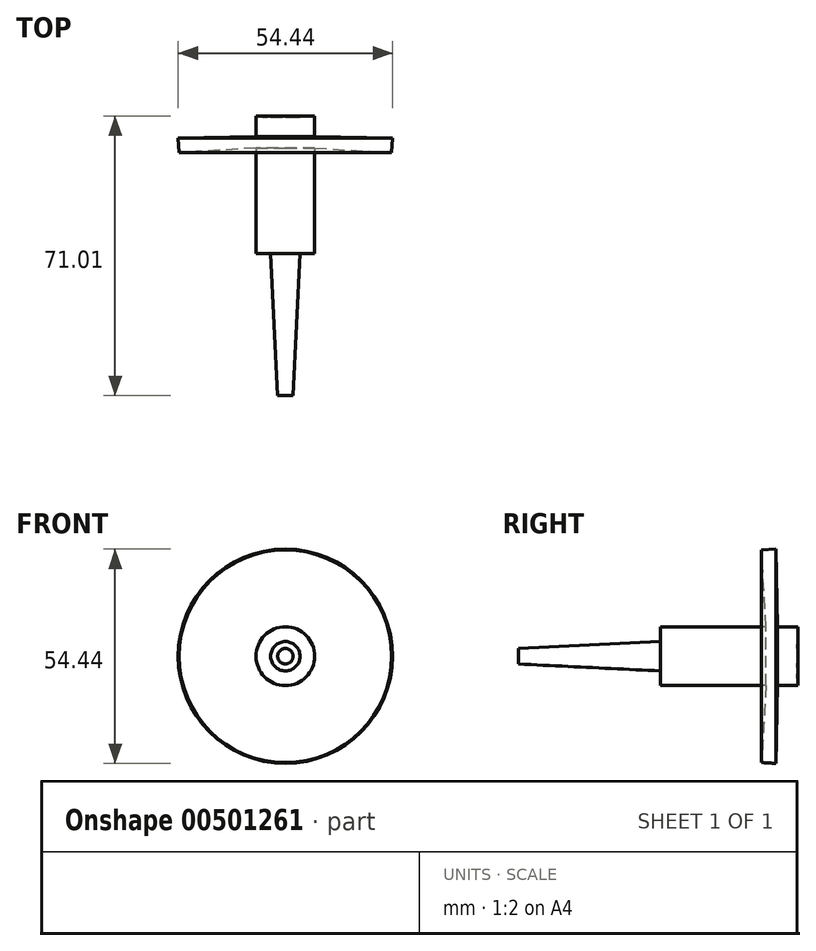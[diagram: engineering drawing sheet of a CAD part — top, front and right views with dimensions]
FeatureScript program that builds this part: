
annotation { "Feature Type Name" : "Feature", "Feature Type Description" : "" }
export const myFeature = defineFeature(function(context is Context, id is Id, definition is map)
    precondition{}
    {
        {
            var Q0;
            Q0=qCreatedBy(makeId("Top.planeOp"),FACE);
            var sketch = newSketch(context, id + "F0", { "sketchPlane" : qUnion([Q0])});
            skLineSegment(sketch, "E0", {"start": v(0, 0) * mm, "end": v(0, 50.8) * mm});
            skArc(sketch, "E1", {"start": v(0, 0) * mm, "mid": v(29.4, 25.4) * mm, "end": v(0, 50.8) * mm});
            skLineSegment(sketch, "E2", {"start": v(7.46, 0) * mm, "end": v(7.46, -34.92) * mm});
            skLineSegment(sketch, "E3", {"start": v(7.46, -34.92) * mm, "end": v(0, -34.92) * mm});
            skLineSegment(sketch, "E4", {"start": v(3.73, -34.92) * mm, "end": v(1.97, -71) * mm});
            skLineSegment(sketch, "E5", {"start": v(1.97, -71) * mm, "end": v(0, -71) * mm});
            skLineSegment(sketch, "E6", {"start": v(0, -71) * mm, "end": v(0, -34.92) * mm});
            skLineSegment(sketch, "E7", {"start": v(7.46, -8.12) * mm, "end": v(27, -9.27) * mm});
            skLineSegment(sketch, "E8", {"start": v(27, -9.27) * mm, "end": v(27.22, -5.6) * mm});
            skLineSegment(sketch, "E9", {"start": v(27.22, -5.6) * mm, "end": v(7.46, -5.23) * mm});
            skLineSegment(sketch, "E10", {"start": v(0, -34.92) * mm, "end": v(0, 0) * mm});
            skSolve(sketch);
        }
        {
            var Q0;
            {var subQ7=sQuery(id+"F0.wireOp",EDGE,"E10");Q0=makeQuery(id+"F0.imprint","IMPRINT",FACE,{"disambiguationData":[TD([[makeQuery(id+"F0.imprint","IMPRINT",EDGE,{"derivedFrom":subQ7}),-1.0]])]});}
            var Q1;
            {var subQ0=sQuery(id+"F0.wireOp",EDGE,"E7");Q1=makeQuery(id+"F0.imprint","IMPRINT",FACE,{"disambiguationData":[TD([[makeQuery(id+"F0.imprint","IMPRINT",EDGE,{"derivedFrom":subQ0}),1.0]])]});}
            var Q2;
            {var subQ2=sQuery(id+"F0.wireOp",EDGE,"E4");Q2=makeQuery(id+"F0.imprint","IMPRINT",FACE,{"disambiguationData":[TD([[makeQuery(id+"F0.imprint","IMPRINT",EDGE,{"derivedFrom":subQ2}),-1.0]])]});}
            var Q3;
            {var subQ0=sQuery(id+"F0.wireOp",EDGE,"E0");Q3=makeQuery(id+"F0.imprint","IMPRINT",FACE,{"disambiguationData":[TD([[makeQuery(id+"F0.imprint","IMPRINT",EDGE,{"derivedFrom":subQ0}),-1.0]])]});}
            var Q4;
            Q4=sQuery(id+"F0.wireOp",EDGE,"E0");
            revolve(context, id + "F1", {"entities" : qUnion([Q0, Q1, Q2, Q3]), "axis" : qUnion([Q4]), "revolveType" : RevolveType.FULL});
        }
    });
